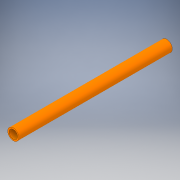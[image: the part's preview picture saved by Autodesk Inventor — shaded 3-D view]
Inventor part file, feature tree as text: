
AUTODESK INVENTOR PART (.ipt)
format: ipt  version: 2018 (Build 220112000, 112)  size: 105,984 bytes
history: native  units: in
note: dims shown in document units (in); Inventor stores cm internally (conversion verified against a paired STEP export)
features: extrude x1, sketch x1
ambient origin geometry x8: Origin, YZ Plane, XZ Plane, XY Plane, X Axis, Y Axis, Z Axis, Center Point
bodies: Solid1 (feature_tree)
feature tree (2):
  extrude  "Extrusion1"  Depth=18.0in
  sketch  "Sketch1"  dims[d0=1.315in d1=1.0in d2=18.0in d3=0.0in]
